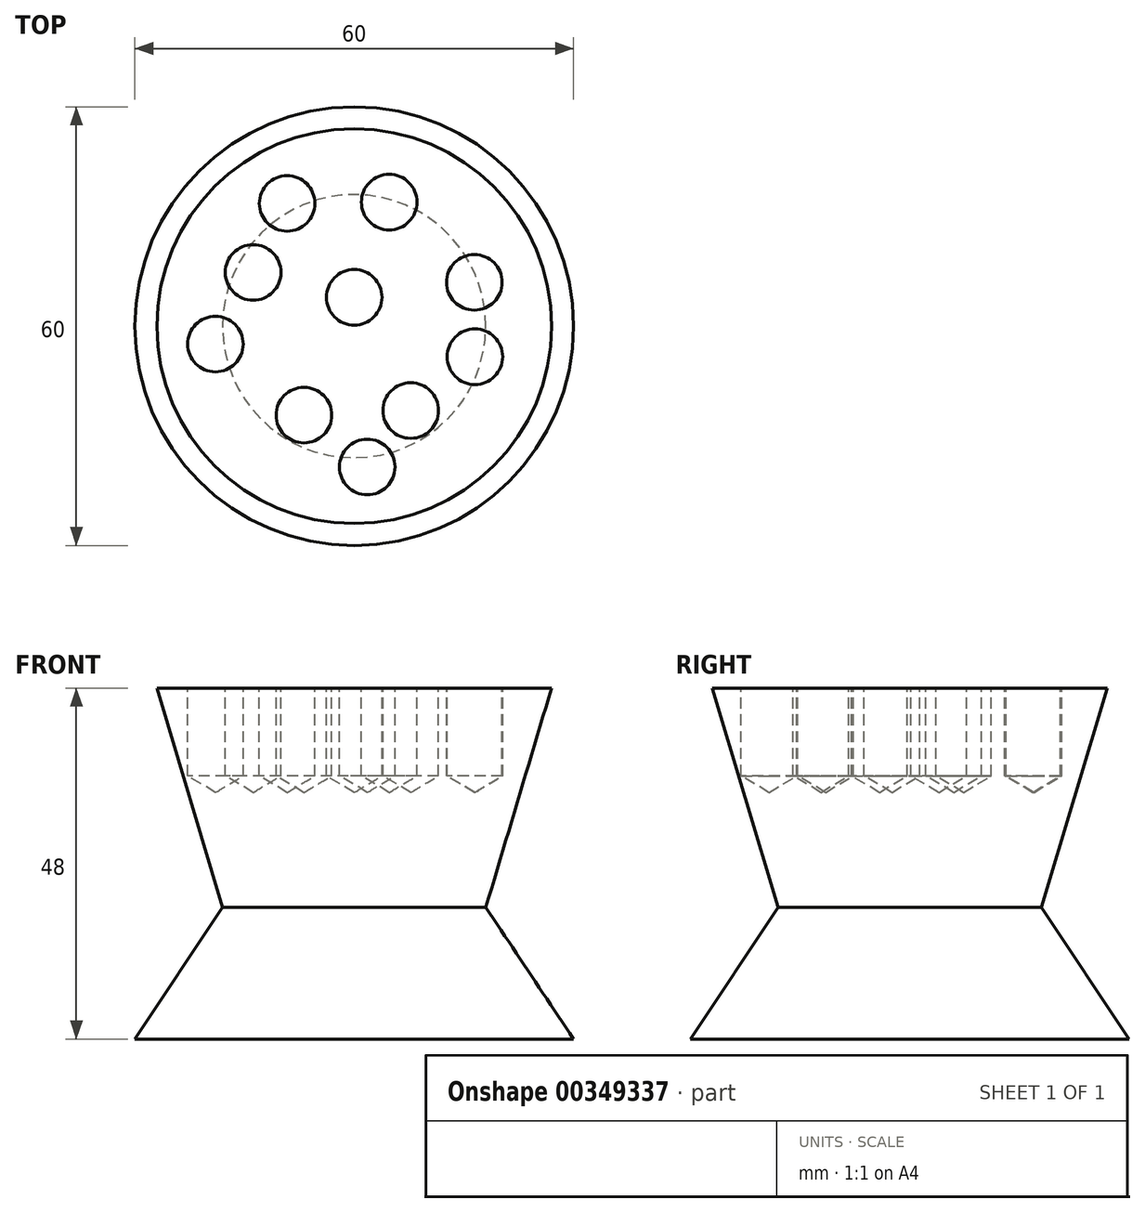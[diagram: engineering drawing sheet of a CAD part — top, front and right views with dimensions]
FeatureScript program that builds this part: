
annotation { "Feature Type Name" : "Feature", "Feature Type Description" : "" }
export const myFeature = defineFeature(function(context is Context, id is Id, definition is map)
    precondition{}
    {
        {
            var Q0;
            Q0=qCreatedBy(makeId("Front.planeOp"),FACE);
            var sketch = newSketch(context, id + "F0", { "sketchPlane" : qUnion([Q0])});
            skLineSegment(sketch, "E0", {"start": v(-30, -48) * mm, "end": v(-18, -30) * mm});
            skLineSegment(sketch, "E1", {"start": v(-18, -30) * mm, "end": v(-27, 0) * mm});
            skLineSegment(sketch, "E2", {"start": v(-27, 0) * mm, "end": v(0, 0) * mm});
            skLineSegment(sketch, "E3", {"start": v(0, 0) * mm, "end": v(0, -48) * mm});
            skLineSegment(sketch, "E4", {"start": v(0, -48) * mm, "end": v(-30, -48) * mm});
            skSolve(sketch);
        }
        {
            var Q0;
            Q0=makeQuery(id+"F0.imprint","IMPRINT",FACE,{"disambiguationData":[TD([[makeQuery(id+"F0.imprint","IMPRINT",EDGE,{"derivedFrom":sQuery(id+"F0.wireOp",EDGE,"E0")}),-1.0]])]});
            var Q1;
            Q1=sQuery(id+"F0.wireOp",EDGE,"E3");
            revolve(context, id + "F1", {"entities" : qUnion([Q0]), "axis" : qUnion([Q1]), "revolveType" : RevolveType.FULL});
        }
        {
            var Q0;
            Q0=qCreatedBy(makeId("Top.planeOp"),FACE);
            var sketch = newSketch(context, id + "F2", { "sketchPlane" : qUnion([Q0])});
            skCircle(sketch, "E5", {"center": v(7.74, -11.54) * mm, "radius": 4.14 * mm});
            skCircle(sketch, "E6", {"center": v(16.43, 6) * mm, "radius": 4.17 * mm});
            skCircle(sketch, "E7", {"center": v(0, 3.95) * mm, "radius": 3.8 * mm});
            skCircle(sketch, "E8", {"center": v(-6.88, -12.16) * mm, "radius": 4 * mm});
            skCircle(sketch, "E9", {"center": v(-18.98, -2.45) * mm, "radius": 3.78 * mm});
            skCircle(sketch, "E10", {"center": v(-9.17, 16.79) * mm, "radius": 3.2 * mm});
            skCircle(sketch, "E11", {"center": v(4.78, 16.96) * mm, "radius": 3.44 * mm});
            skSolve(sketch);
        }
        {
            var Q0;
            Q0=sQuery(id+"F2.wireOp",VERTEX,"E11.center");
            var Q1;
            Q1=sQuery(id+"F2.wireOp",VERTEX,"E7.center");
            var Q2;
            Q2=sQuery(id+"F2.wireOp",VERTEX,"E6.center");
            var Q3;
            Q3=sQuery(id+"F2.wireOp",VERTEX,"E10.center");
            var Q4;
            Q4=sQuery(id+"F2.wireOp",VERTEX,"E5.center");
            var Q5;
            Q5=sQuery(id+"F2.wireOp",VERTEX,"E8.center");
            var Q6;
            Q6=sQuery(id+"F2.wireOp",VERTEX,"E9.center");
            var Q7;
            Q7=makeQuery(id+"F1.opRevolve","SWEPT_BODY",BODY,{"disambiguationData":[OSD([sQuery(id+"F0.wireOp",EDGE,"E0"),sQuery(id+"F0.wireOp",EDGE,"E1"),sQuery(id+"F0.wireOp",EDGE,"E2"),sQuery(id+"F0.wireOp",EDGE,"E3"),sQuery(id+"F0.wireOp",EDGE,"E4")])]});
            hole(context, id + "F3", {"style" : HoleStyle.SIMPLE, "endStyle" : HoleEndStyle.BLIND, "holeDiameter" : 7.6 * mm, "holeDepth" : 12 * mm, "isTappedThrough" : true, "tappedDepth" : 12 * mm, "tapClearance" : 3, "locations" : qUnion([Q0, Q1, Q2, Q3, Q4, Q5, Q6]), "scope" : qUnion([Q7])});
        }
        {
            var Q0;
            Q0=qCreatedBy(makeId("Top.planeOp"),FACE);
            var sketch = newSketch(context, id + "F4", { "sketchPlane" : qUnion([Q0])});
            skCircle(sketch, "E12", {"center": v(1.78, -19.26) * mm, "radius": 3.9 * mm});
            skCircle(sketch, "E13", {"center": v(16.5, -4.18) * mm, "radius": 3.84 * mm});
            skCircle(sketch, "E14", {"center": v(-13.83, 7.35) * mm, "radius": 3.76 * mm});
            skSolve(sketch);
        }
        {
            var Q0;
            Q0=sQuery(id+"F4.wireOp",VERTEX,"E14.center");
            var Q1;
            Q1=sQuery(id+"F4.wireOp",VERTEX,"E12.center");
            var Q2;
            Q2=sQuery(id+"F4.wireOp",VERTEX,"E13.center");
            var Q3;
            Q3=makeQuery(id+"F1.opRevolve","SWEPT_BODY",BODY,{"disambiguationData":[OSD([sQuery(id+"F0.wireOp",EDGE,"E0"),sQuery(id+"F0.wireOp",EDGE,"E1"),sQuery(id+"F0.wireOp",EDGE,"E2"),sQuery(id+"F0.wireOp",EDGE,"E3"),sQuery(id+"F0.wireOp",EDGE,"E4")])]});
            hole(context, id + "F5", {"style" : HoleStyle.SIMPLE, "endStyle" : HoleEndStyle.BLIND, "holeDiameter" : 7.6 * mm, "holeDepth" : 12 * mm, "isTappedThrough" : true, "tappedDepth" : 12 * mm, "tapClearance" : 3, "locations" : qUnion([Q0, Q1, Q2]), "scope" : qUnion([Q3])});
        }
    });
